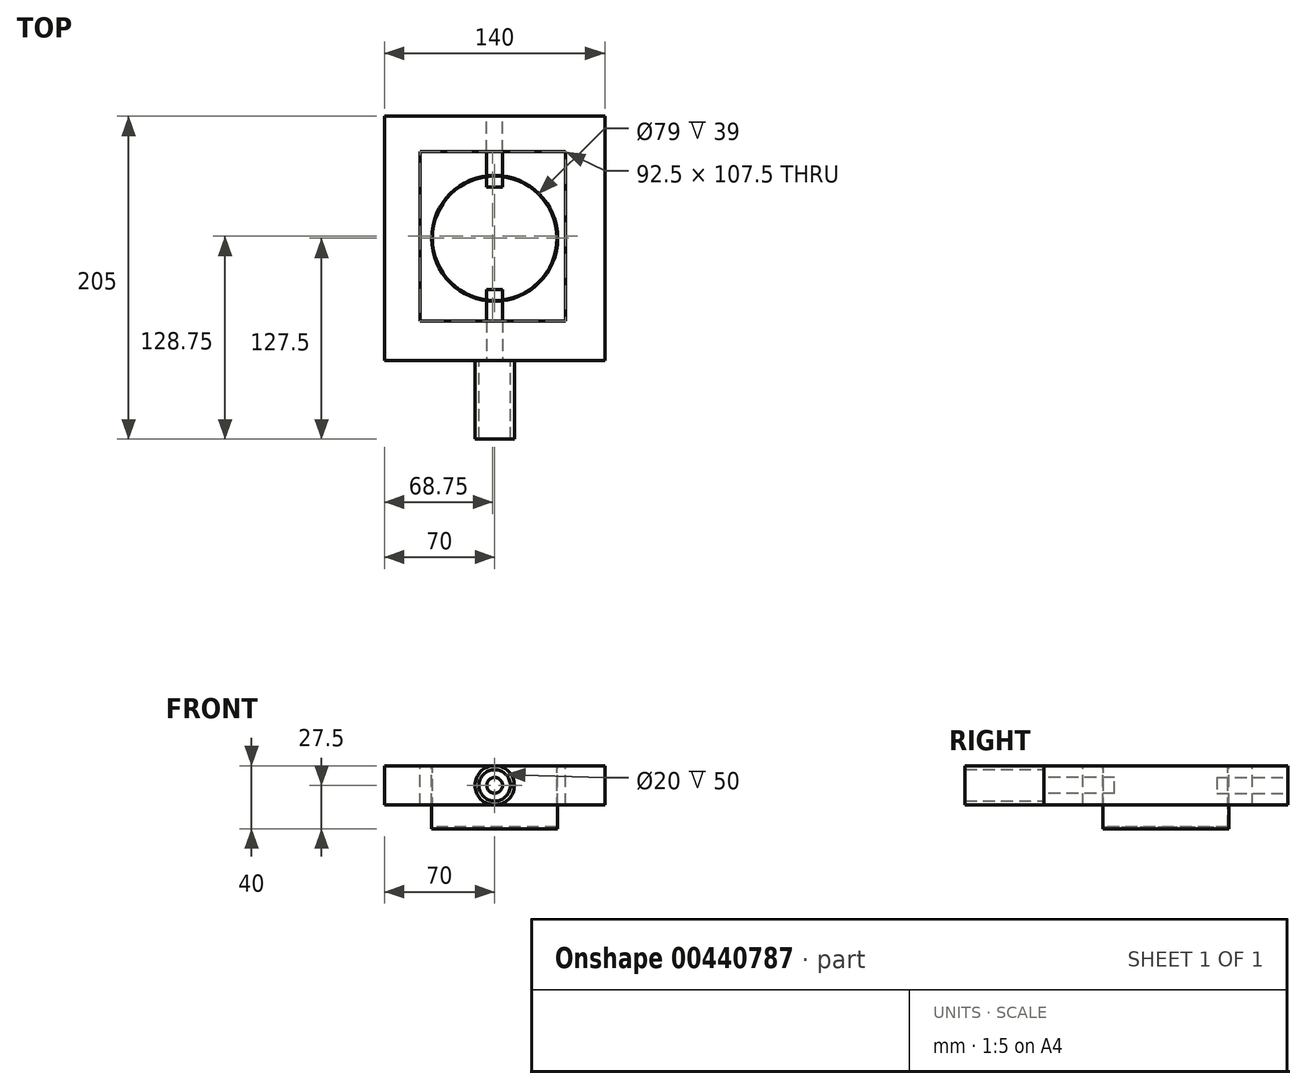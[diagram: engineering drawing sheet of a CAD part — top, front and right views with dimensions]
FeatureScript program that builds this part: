
annotation { "Feature Type Name" : "Feature", "Feature Type Description" : "" }
export const myFeature = defineFeature(function(context is Context, id is Id, definition is map)
    precondition{}
    {
        {
            var Q0;
            Q0=qCreatedBy(makeId("Front.planeOp"),FACE);
            var sketch = newSketch(context, id + "F0", { "sketchPlane" : qUnion([Q0])});
            skLineSegment(sketch, "E0.bottom", {"start": v(0, 0) * mm, "end": v(140, 0) * mm});
            skLineSegment(sketch, "E0.top", {"start": v(0, 25) * mm, "end": v(140, 25) * mm});
            skLineSegment(sketch, "E0.left", {"start": v(0, 0) * mm, "end": v(0, 25) * mm});
            skLineSegment(sketch, "E0.right", {"start": v(140, 0) * mm, "end": v(140, 25) * mm});
            skSolve(sketch);
        }
        {
            var Q0;
            Q0 = qSketchRegion(id + "F0", true);
            extrude(context, id + "F1", {"entities" : qUnion([Q0]), "depth" : 155 * mm});
        }
        {
            var Q0;
            Q0=makeQuery(id+"F1.opExtrude","SWEPT_FACE",FACE,{"disambiguationData":[OSD([sQuery(id+"F0.wireOp",EDGE,"E0.top")])]});
            var sketch = newSketch(context, id + "F2", { "sketchPlane" : qUnion([Q0])});
            skCircle(sketch, "E1", {"center": v(70, -77.5) * mm, "radius": 40 * mm});
            skCircle(sketch, "E2", {"center": v(70, -77.5) * mm, "radius": 39.5 * mm});
            skSolve(sketch);
        }
        {
            var Q0;
            Q0=makeQuery(id+"F2.imprint","IMPRINT",FACE,{"disambiguationData":[TD([[makeQuery(id+"F2.imprint","IMPRINT",EDGE,{"derivedFrom":sQuery(id+"F2.wireOp",EDGE,"E2")}),1.0]])]});
            var Q1;
            Q1=makeQuery(id+"F2.imprint","IMPRINT",FACE,{"disambiguationData":[TD([[makeQuery(id+"F2.imprint","IMPRINT",EDGE,{"derivedFrom":sQuery(id+"F2.wireOp",EDGE,"E1")}),1.0]])]});
            extrude(context, id + "F3", {"entities" : qUnion([Q0, Q1]), "operationType" : NewBodyOperationType.ADD, "oppositeDirection" : true, "depth" : 40 * mm});
        }
        {
            var Q0;
            Q0=makeQuery(id+"F1.opExtrude","SWEPT_FACE",FACE,{"disambiguationData":[OSD([sQuery(id+"F0.wireOp",EDGE,"E0.top")])]});
            var sketch = newSketch(context, id + "F4", { "sketchPlane" : qUnion([Q0])});
            skCircle(sketch, "E3", {"center": v(70, -77.5) * mm, "radius": 39.5 * mm});
            skPoint(sketch, "E3.centerSnap0", {"position": v(70, 0) * mm});
            skSolve(sketch);
        }
        {
            var Q0;
            Q0=makeQuery(id+"F4.imprint","IMPRINT",FACE,{"disambiguationData":[TD([[makeQuery(id+"F4.imprint","IMPRINT",EDGE,{"derivedFrom":sQuery(id+"F4.wireOp",EDGE,"E3")}),1.0]])]});
            extrude(context, id + "F5", {"entities" : qUnion([Q0]), "operationType" : NewBodyOperationType.REMOVE, "oppositeDirection" : true, "depth" : 39 * mm});
        }
        {
            var Q0;
            Q0=makeQuery(id+"F1.opExtrude","SWEPT_FACE",FACE,{"disambiguationData":[OSD([sQuery(id+"F0.wireOp",EDGE,"E0.top")])]});
            var sketch = newSketch(context, id + "F6", { "sketchPlane" : qUnion([Q0])});
            skLineSegment(sketch, "E4.bottom", {"start": v(22.5, -22.5) * mm, "end": v(115, -22.5) * mm});
            skLineSegment(sketch, "E4.top", {"start": v(22.5, -130) * mm, "end": v(115, -130) * mm});
            skLineSegment(sketch, "E4.left", {"start": v(22.5, -22.5) * mm, "end": v(22.5, -130) * mm});
            skLineSegment(sketch, "E4.right", {"start": v(115, -22.5) * mm, "end": v(115, -130) * mm});
            skCircle(sketch, "E5", {"center": v(70, -77.5) * mm, "radius": 40 * mm});
            skSolve(sketch);
        }
        {
            var Q0;
            Q0=makeQuery(id+"F6.imprint","IMPRINT",FACE,{"disambiguationData":[TD([[makeQuery(id+"F6.imprint","IMPRINT",EDGE,{"derivedFrom":sQuery(id+"F6.wireOp",EDGE,"E4.bottom")}),-1.0]])]});
            extrude(context, id + "F7", {"entities" : qUnion([Q0]), "operationType" : NewBodyOperationType.REMOVE, "oppositeDirection" : true, "depth" : 95 * mm});
        }
        {
            var Q0;
            Q0=makeQuery(id+"F1.opExtrude","CAP_FACE",FACE,{"disambiguationData":[OSD([sQuery(id+"F0.wireOp",EDGE,"E0.bottom"),sQuery(id+"F0.wireOp",EDGE,"E0.top"),sQuery(id+"F0.wireOp",EDGE,"E0.left"),sQuery(id+"F0.wireOp",EDGE,"E0.right")])],"isStart":false});
            var sketch = newSketch(context, id + "F8", { "sketchPlane" : qUnion([Q0])});
            skCircle(sketch, "E6", {"center": v(70, 12.5) * mm, "radius": 5 * mm});
            skPoint(sketch, "E6.centerSnap0", {"position": v(0, 12.5) * mm});
            skPoint(sketch, "E6.centerSnap1", {"position": v(70, 0) * mm});
            skSolve(sketch);
        }
        {
            var Q0;
            Q0=makeQuery(id+"F8.imprint","IMPRINT",FACE,{"disambiguationData":[TD([[makeQuery(id+"F8.imprint","IMPRINT",EDGE,{"derivedFrom":sQuery(id+"F8.wireOp",EDGE,"E6")}),1.0]])]});
            extrude(context, id + "F9", {"entities" : qUnion([Q0]), "oppositeDirection" : true, "depth" : 45 * mm});
        }
        {
            var Q0;
            Q0=makeQuery(id+"F1.opExtrude","CAP_FACE",FACE,{"disambiguationData":[OSD([sQuery(id+"F0.wireOp",EDGE,"E0.bottom"),sQuery(id+"F0.wireOp",EDGE,"E0.top"),sQuery(id+"F0.wireOp",EDGE,"E0.left"),sQuery(id+"F0.wireOp",EDGE,"E0.right")])],"isStart":true});
            var sketch = newSketch(context, id + "F10", { "sketchPlane" : qUnion([Q0])});
            skCircle(sketch, "E7", {"center": v(-70, 12.5) * mm, "radius": 5 * mm});
            skPoint(sketch, "E7.centerSnap0", {"position": v(-140, 12.5) * mm});
            skPoint(sketch, "E7.centerSnap1", {"position": v(-70, 0) * mm});
            skSolve(sketch);
        }
        {
            var Q0;
            Q0=makeQuery(id+"F10.imprint","IMPRINT",FACE,{"disambiguationData":[TD([[makeQuery(id+"F10.imprint","IMPRINT",EDGE,{"derivedFrom":sQuery(id+"F10.wireOp",EDGE,"E7")}),1.0]])]});
            extrude(context, id + "F11", {"entities" : qUnion([Q0]), "oppositeDirection" : true, "depth" : 45 * mm});
        }
        {
            var Q0;
            Q0=makeQuery(id+"F1.opExtrude","CAP_FACE",FACE,{"disambiguationData":[OSD([sQuery(id+"F0.wireOp",EDGE,"E0.bottom"),sQuery(id+"F0.wireOp",EDGE,"E0.top"),sQuery(id+"F0.wireOp",EDGE,"E0.left"),sQuery(id+"F0.wireOp",EDGE,"E0.right")])],"isStart":false});
            var sketch = newSketch(context, id + "F12", { "sketchPlane" : qUnion([Q0])});
            skCircle(sketch, "E8", {"center": v(70, 12.5) * mm, "radius": 10 * mm});
            skPoint(sketch, "E8.centerSnap0", {"position": v(0, 12.5) * mm});
            skPoint(sketch, "E8.centerSnap1", {"position": v(70, 0) * mm});
            skCircle(sketch, "E9", {"center": v(70, 12.5) * mm, "radius": 12.5 * mm});
            skSolve(sketch);
        }
        {
            var Q0;
            Q0=makeQuery(id+"F12.imprint","IMPRINT",FACE,{"disambiguationData":[TD([[makeQuery(id+"F12.imprint","IMPRINT",EDGE,{"derivedFrom":sQuery(id+"F12.wireOp",EDGE,"E8")}),-1.0]])]});
            extrude(context, id + "F13", {"entities" : qUnion([Q0]), "operationType" : NewBodyOperationType.ADD, "depth" : 50 * mm});
        }
    });
